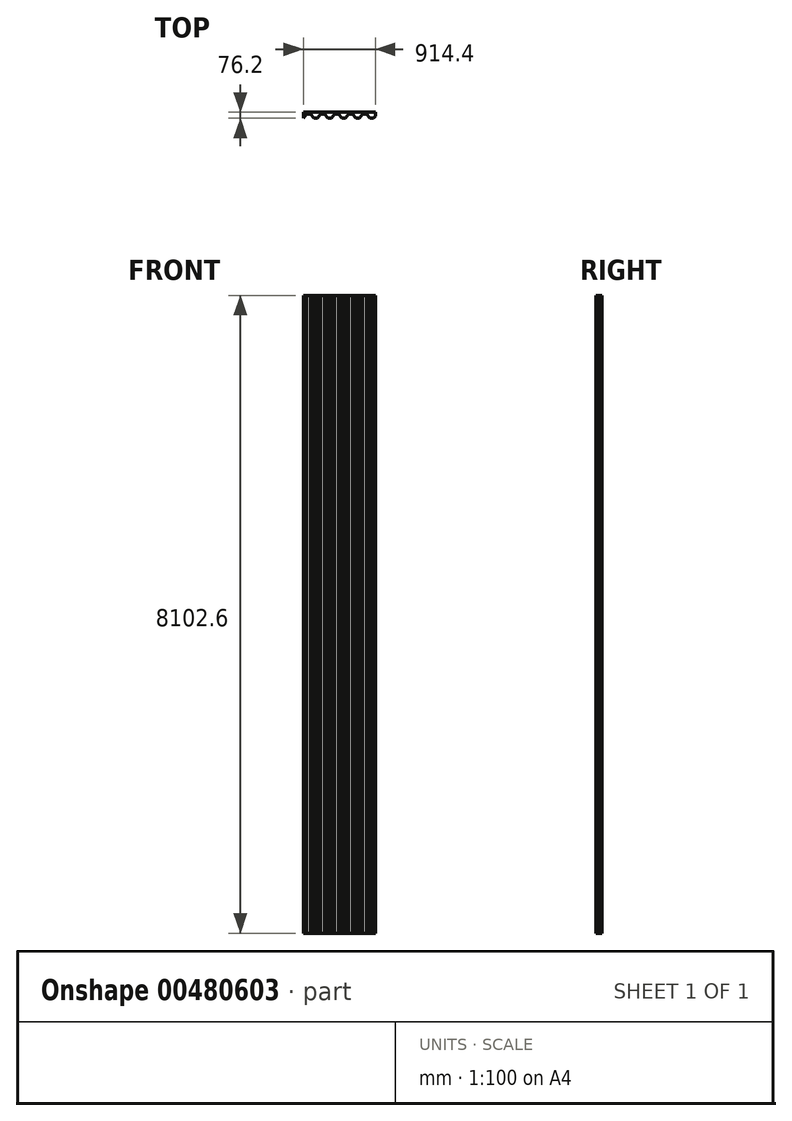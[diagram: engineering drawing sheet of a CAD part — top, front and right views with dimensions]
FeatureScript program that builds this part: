
annotation { "Feature Type Name" : "Feature", "Feature Type Description" : "" }
export const myFeature = defineFeature(function(context is Context, id is Id, definition is map)
    precondition{}
    {
        {
            var Q0;
            Q0=qCreatedBy(makeId("Top.planeOp"),FACE);
            var sketch = newSketch(context, id + "F0", { "sketchPlane" : qUnion([Q0])});
            skLineSegment(sketch, "E0.bottom", {"start": v(457.2, -50.8) * mm, "end": v(-457.2, -50.8) * mm});
            skLineSegment(sketch, "E0.top", {"start": v(457.2, 50.8) * mm, "end": v(-457.2, 50.8) * mm});
            skLineSegment(sketch, "E0.left", {"start": v(457.2, -50.8) * mm, "end": v(457.2, 50.8) * mm});
            skLineSegment(sketch, "E0.right", {"start": v(-457.2, -50.8) * mm, "end": v(-457.2, 50.8) * mm});
            skPoint(sketch, "E0.middle", {"position": v(0, 0) * mm});
            skSolve(sketch);
        }
        {
            var Q0;
            Q0=qSketchRegion(id+"F0",true);
            extrude(context, id + "F1", {"entities" : qUnion([Q0]), "depth" : 8102.6 * mm});
        }
        {
            var Q0;
            Q0=makeQuery(id+"F1.opExtrude","CAP_FACE",FACE,{"disambiguationData":[OSD([sQuery(id+"F0.wireOp",EDGE,"E0.bottom"),sQuery(id+"F0.wireOp",EDGE,"E0.top"),sQuery(id+"F0.wireOp",EDGE,"E0.left"),sQuery(id+"F0.wireOp",EDGE,"E0.right")])],"isStart":false});
            var sketch = newSketch(context, id + "F2", { "sketchPlane" : qUnion([Q0])});
            skLineSegment(sketch, "E1", {"start": v(-457.2, 0) * mm, "end": v(-457.2, 25.4) * mm, "construction": true});
            skLineSegment(sketch, "E2", {"start": v(-457.2, 0) * mm, "end": v(-457.2, -25.4) * mm, "construction": true});
            skLineSegment(sketch, "E3", {"start": v(-457.2, -25.4) * mm, "end": v(-414.57, 25.4) * mm});
            skLineSegment(sketch, "E4", {"start": v(-414.57, 25.4) * mm, "end": v(-363.77, 25.4) * mm});
            skLineSegment(sketch, "E5", {"start": v(-363.77, 25.4) * mm, "end": v(-321.15, -25.4) * mm});
            skLineSegment(sketch, "E6", {"start": v(-321.15, -25.4) * mm, "end": v(-279.4, -25.4) * mm});
            skLineSegment(sketch, "E7.1.0.0", {"start": v(-279.4, -25.4) * mm, "end": v(-236.77, 25.4) * mm});
            skLineSegment(sketch, "E7.1.0.1", {"start": v(-236.77, 25.4) * mm, "end": v(-185.97, 25.4) * mm});
            skLineSegment(sketch, "E7.1.0.2", {"start": v(-185.97, 25.4) * mm, "end": v(-143.35, -25.4) * mm});
            skLineSegment(sketch, "E7.1.0.3", {"start": v(-143.35, -25.4) * mm, "end": v(-101.6, -25.4) * mm});
            skLineSegment(sketch, "E7.2.0.0", {"start": v(-101.6, -25.4) * mm, "end": v(-58.97, 25.4) * mm});
            skLineSegment(sketch, "E7.2.0.1", {"start": v(-58.97, 25.4) * mm, "end": v(-8.17, 25.4) * mm});
            skLineSegment(sketch, "E7.2.0.2", {"start": v(-8.17, 25.4) * mm, "end": v(34.45, -25.4) * mm});
            skLineSegment(sketch, "E7.2.0.3", {"start": v(34.45, -25.4) * mm, "end": v(76.2, -25.4) * mm});
            skLineSegment(sketch, "E7.3.0.0", {"start": v(76.2, -25.4) * mm, "end": v(118.83, 25.4) * mm});
            skLineSegment(sketch, "E7.3.0.1", {"start": v(118.83, 25.4) * mm, "end": v(169.63, 25.4) * mm});
            skLineSegment(sketch, "E7.3.0.2", {"start": v(169.63, 25.4) * mm, "end": v(212.25, -25.4) * mm});
            skLineSegment(sketch, "E7.3.0.3", {"start": v(212.25, -25.4) * mm, "end": v(254, -25.4) * mm});
            skLineSegment(sketch, "E7.4.0.0", {"start": v(254, -25.4) * mm, "end": v(296.63, 25.4) * mm});
            skLineSegment(sketch, "E7.4.0.1", {"start": v(296.63, 25.4) * mm, "end": v(347.43, 25.4) * mm});
            skLineSegment(sketch, "E7.4.0.2", {"start": v(347.43, 25.4) * mm, "end": v(390.05, -25.4) * mm});
            skLineSegment(sketch, "E7.4.0.3", {"start": v(390.05, -25.4) * mm, "end": v(431.8, -25.4) * mm});
            skLineSegment(sketch, "E7.5.0.0", {"start": v(431.8, -25.4) * mm, "end": v(457.2, 4.87) * mm});
            skLineSegment(sketch, "E7.direction1", {"start": v(-457.2, -25.4) * mm, "end": v(-279.4, -25.4) * mm, "construction": true});
            skPoint(sketch, "E8", {"position": v(457.2, 4.87) * mm});
            skPoint(sketch, "E9.orphan", {"position": v(474.43, 25.4) * mm});
            skSolve(sketch);
        }
        {
            var Q0;
            Q0=qSketchRegion(id+"F2",true);
            var Q1;
            {var subQ2=sQuery(id+"F2.wireOp",EDGE,"E3");Q1=makeQuery(id+"F2.imprint","IMPRINT",FACE,{"disambiguationData":[TD([[makeQuery(id+"F2.imprint","IMPRINT",EDGE,{"derivedFrom":subQ2}),-1.0]])]});}
            extrude(context, id + "F3", {"entities" : qUnion([Q0, Q1]), "operationType" : NewBodyOperationType.REMOVE, "endBound" : BoundingType.THROUGH_ALL, "oppositeDirection" : true, "depth" : 25.4 * mm});
        }
    });
